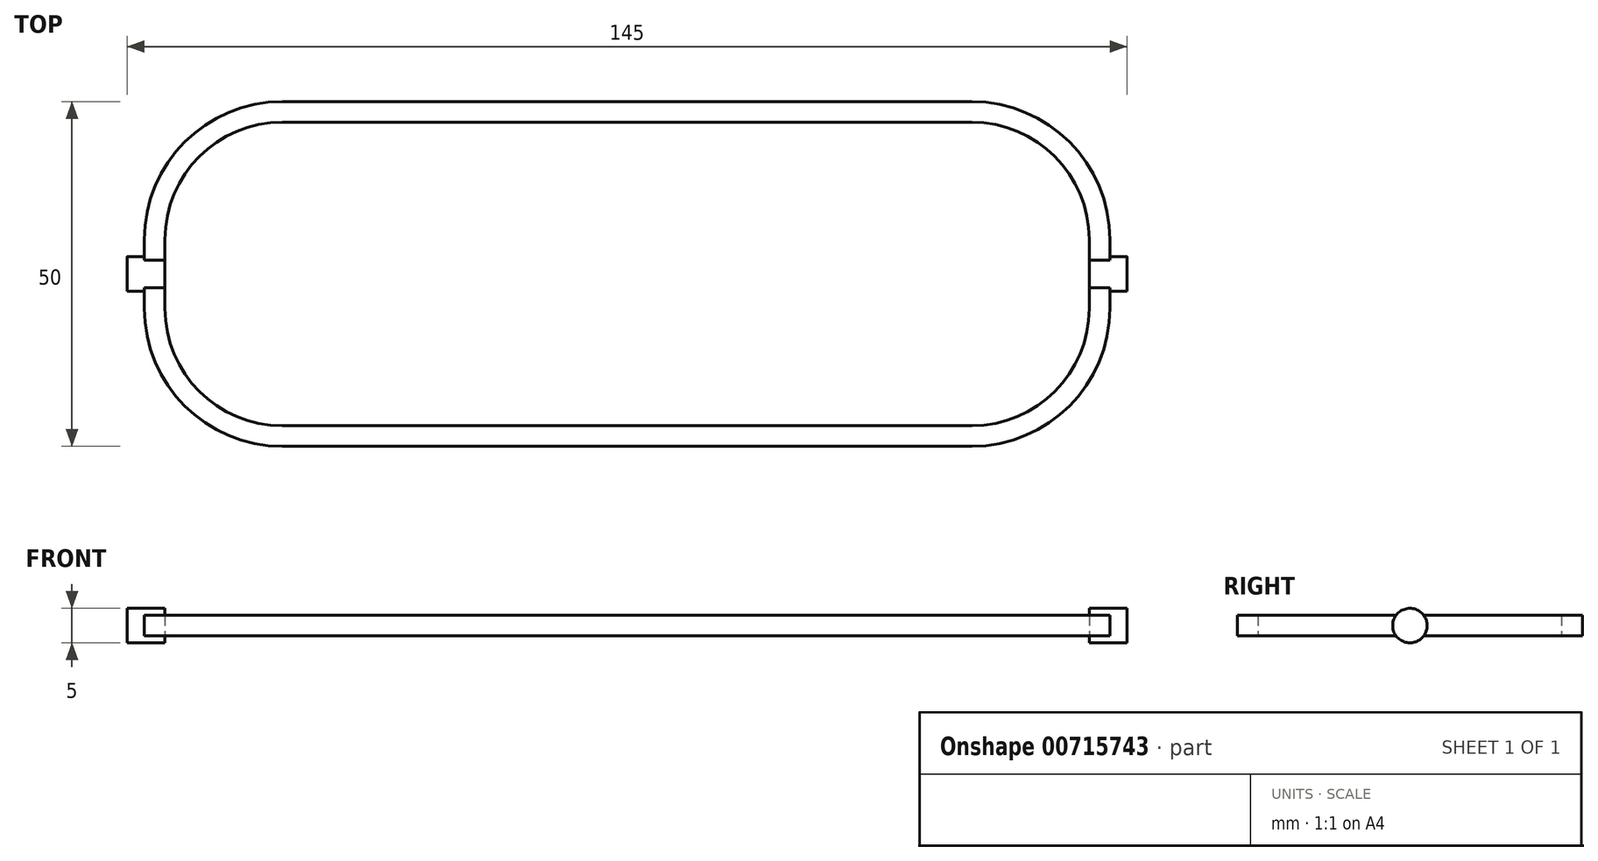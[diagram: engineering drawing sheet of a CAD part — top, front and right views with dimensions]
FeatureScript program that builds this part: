
annotation { "Feature Type Name" : "Feature", "Feature Type Description" : "" }
export const myFeature = defineFeature(function(context is Context, id is Id, definition is map)
    precondition{}
    {
        {
            var Q0;
            Q0=qCreatedBy(makeId("Top.planeOp"),FACE);
            var sketch = newSketch(context, id + "F0", { "sketchPlane" : qUnion([Q0])});
            skLineSegment(sketch, "E0.bottom", {"start": v(-50, 25) * mm, "end": v(50, 25) * mm});
            skLineSegment(sketch, "E0.top", {"start": v(-50, -25) * mm, "end": v(50, -25) * mm});
            skLineSegment(sketch, "E0.left", {"start": v(-70, 5) * mm, "end": v(-70, -5) * mm});
            skLineSegment(sketch, "E0.right", {"start": v(70, 5) * mm, "end": v(70, -5) * mm});
            skPoint(sketch, "E1.visualSharp", {"position": v(-70, 25) * mm});
            skArc(sketch, "E1.filletArc", {"start": v(-50, 25) * mm, "mid": v(-64.14, 19.14) * mm, "end": v(-70, 5) * mm});
            skPoint(sketch, "E2.visualSharp", {"position": v(-70, -25) * mm});
            skArc(sketch, "E2.filletArc", {"start": v(-70, -5) * mm, "mid": v(-64.14, -19.14) * mm, "end": v(-50, -25) * mm});
            skPoint(sketch, "E3.visualSharp", {"position": v(70, -25) * mm});
            skArc(sketch, "E3.filletArc", {"start": v(50, -25) * mm, "mid": v(64.14, -19.14) * mm, "end": v(70, -5) * mm});
            skPoint(sketch, "E4.visualSharp", {"position": v(70, 25) * mm});
            skArc(sketch, "E4.filletArc", {"start": v(70, 5) * mm, "mid": v(64.14, 19.14) * mm, "end": v(50, 25) * mm});
            skLineSegment(sketch, "E5.0", {"start": v(-67, 5) * mm, "end": v(-67, -5) * mm});
            skArc(sketch, "E5.1", {"start": v(-50, 22) * mm, "mid": v(-62.02, 17.02) * mm, "end": v(-67, 5) * mm});
            skArc(sketch, "E5.2", {"start": v(-67, -5) * mm, "mid": v(-62.02, -17.02) * mm, "end": v(-50, -22) * mm});
            skLineSegment(sketch, "E5.3", {"start": v(-50, 22) * mm, "end": v(50, 22) * mm});
            skLineSegment(sketch, "E5.4", {"start": v(-50, -22) * mm, "end": v(50, -22) * mm});
            skArc(sketch, "E5.5", {"start": v(50, -22) * mm, "mid": v(62.02, -17.02) * mm, "end": v(67, -5) * mm});
            skLineSegment(sketch, "E5.6", {"start": v(67, 5) * mm, "end": v(67, -5) * mm});
            skArc(sketch, "E5.7", {"start": v(67, 5) * mm, "mid": v(62.02, 17.02) * mm, "end": v(50, 22) * mm});
            skSolve(sketch);
        }
        {
            var Q0;
            Q0 = qSketchRegion(id + "F0", true);
            extrude(context, id + "F1", {"entities" : qUnion([Q0]), "depth" : 3 * mm, "offsetDistance" : 25 * mm, "symmetric" : true});
        }
        {
            var Q0;
            Q0=qCreatedBy(makeId("Right.planeOp"),FACE);
            var sketch = newSketch(context, id + "F2", { "sketchPlane" : qUnion([Q0])});
            skCircle(sketch, "E6", {"center": v(0, 0) * mm, "radius": 2.5 * mm});
            skSolve(sketch);
        }
        {
            var Q0;
            Q0 = qSketchRegion(id + "F2", true);
            extrude(context, id + "F3", {"entities" : qUnion([Q0]), "operationType" : NewBodyOperationType.ADD, "depth" : (145 / 2) * mm, "offsetDistance" : 25 * mm});
        }
        {
            var Q0;
            Q0 = qSketchRegion(id + "F2", true);
            var Q1;
            {var subQ1=sQuery(id+"F0.wireOp",EDGE,"E5.6");var subQ2=sQuery(id+"F0.wireOp",EDGE,"E5.5");Q1=makeQuery(id+"F3.boolean.opBoolean","SPLIT",FACE,{"disambiguationData":[TD([makeQuery(id+"F1.opExtrude","SWEPT_FACE",FACE,{"disambiguationData":[OSD([subQ2])]})])],"derivedFrom":makeQuery(id+"F1.opExtrude","SWEPT_FACE",FACE,{"disambiguationData":[OSD([subQ1])]})});}
            extrude(context, id + "F4", {"entities" : qUnion([Q0]), "operationType" : NewBodyOperationType.REMOVE, "endBound" : BoundingType.UP_TO_SURFACE, "depth" : 25 * mm, "endBoundEntityFace" : qUnion([Q1]), "offsetDistance" : 25 * mm});
        }
        {
            var Q0;
            Q0=makeQuery(id+"F1.opExtrude","SWEPT_BODY",BODY,{"disambiguationData":[OSD([sQuery(id+"F0.wireOp",EDGE,"E0.bottom"),sQuery(id+"F0.wireOp",EDGE,"E0.top"),sQuery(id+"F0.wireOp",EDGE,"E0.left"),sQuery(id+"F0.wireOp",EDGE,"E0.right"),sQuery(id+"F0.wireOp",EDGE,"dbc793f4-2267-4797-88a7-d1d1bf787b45.0"),sQuery(id+"F0.wireOp",EDGE,"dbc793f4-2267-4797-88a7-d1d1bf787b45.1"),sQuery(id+"F0.wireOp",EDGE,"dbc793f4-2267-4797-88a7-d1d1bf787b45.2"),sQuery(id+"F0.wireOp",EDGE,"dbc793f4-2267-4797-88a7-d1d1bf787b45.3")])]});
            var Q1;
            Q1=qCreatedBy(makeId("Right.planeOp"),FACE);
            mirror(context, id + "F5", {"operationType" : NewBodyOperationType.ADD, "entities" : qUnion([Q0]), "mirrorPlane" : qUnion([Q1])});
        }
    });
